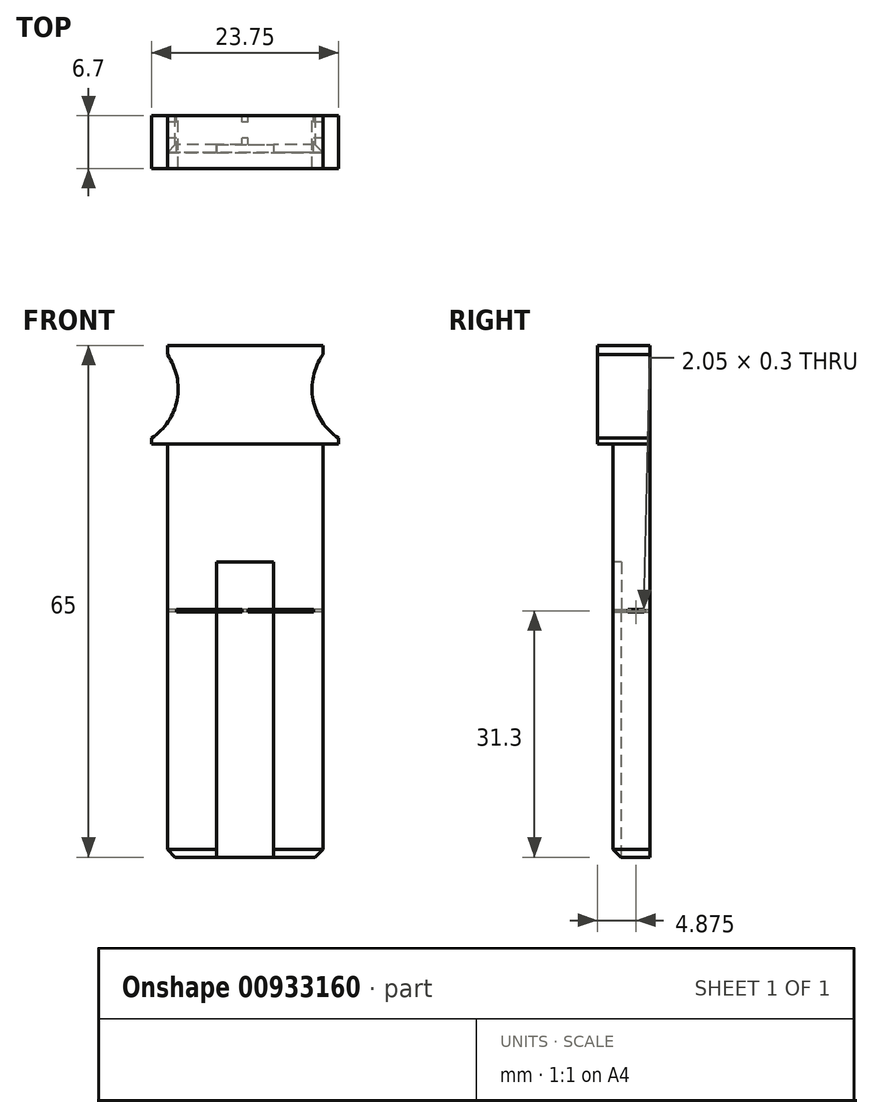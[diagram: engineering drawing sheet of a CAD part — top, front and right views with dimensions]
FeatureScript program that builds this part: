
annotation { "Feature Type Name" : "Feature", "Feature Type Description" : "" }
export const myFeature = defineFeature(function(context is Context, id is Id, definition is map)
    precondition{}
    {
        {
            var Q0;
            Q0=qCreatedBy(makeId("Front.planeOp"),FACE);
            var sketch = newSketch(context, id + "F0", { "sketchPlane" : qUnion([Q0])});
            skLineSegment(sketch, "E0.bottom", {"start": v(0, 0) * mm, "end": v(19.75, 0) * mm});
            skLineSegment(sketch, "E0.top", {"start": v(0, 65) * mm, "end": v(19.75, 65) * mm});
            skLineSegment(sketch, "E0.left", {"start": v(0, 0) * mm, "end": v(0, 65) * mm});
            skLineSegment(sketch, "E0.right", {"start": v(19.75, 0) * mm, "end": v(19.75, 65) * mm});
            skLineSegment(sketch, "E1", {"start": v(9.87, 65) * mm, "end": v(9.87, 0) * mm, "construction": true});
            skPoint(sketch, "E2", {"position": v(9.87, 38.5) * mm});
            skLineSegment(sketch, "E3", {"start": v(-7.67, 31.3) * mm, "end": v(34.9, 31.3) * mm, "construction": true});
            skLineSegment(sketch, "E4", {"start": v(0, 31.15) * mm, "end": v(0, 31.45) * mm});
            skCircle(sketch, "E5", {"center": v(25.88, 59.5) * mm, "radius": 7.5 * mm});
            skCircle(sketch, "E6.MirrorC", {"center": v(-6.13, 59.5) * mm, "radius": 7.5 * mm});
            skLineSegment(sketch, "E7.bottom", {"start": v(0, 31.45) * mm, "end": v(9.47, 31.45) * mm});
            skLineSegment(sketch, "E7.top", {"start": v(0, 31.45) * mm, "end": v(9.47, 31.45) * mm});
            skLineSegment(sketch, "E7.left", {"start": v(0, 31.45) * mm, "end": v(0, 31.45) * mm});
            skLineSegment(sketch, "E7.right", {"start": v(9.47, 31.45) * mm, "end": v(9.47, 31.45) * mm});
            skLineSegment(sketch, "E8", {"start": v(9.47, 31.45) * mm, "end": v(9.47, 31.15) * mm});
            skLineSegment(sketch, "E9", {"start": v(9.47, 31.15) * mm, "end": v(0, 31.15) * mm});
            skLineSegment(sketch, "E10", {"start": v(0, 31.45) * mm, "end": v(0, 31.15) * mm});
            skLineSegment(sketch, "E11.MirrorCS", {"start": v(19.75, 31.45) * mm, "end": v(10.28, 31.45) * mm});
            skLineSegment(sketch, "E12.MirrorCS", {"start": v(10.27, 31.45) * mm, "end": v(10.27, 31.15) * mm});
            skLineSegment(sketch, "E13.MirrorCS", {"start": v(10.28, 31.15) * mm, "end": v(19.75, 31.15) * mm});
            skLineSegment(sketch, "E14.MirrorCS", {"start": v(19.75, 31.45) * mm, "end": v(19.75, 31.15) * mm});
            skLineSegment(sketch, "E15.bottom", {"start": v(0, 52.5) * mm, "end": v(-2, 52.5) * mm});
            skLineSegment(sketch, "E15.top", {"start": v(0, 65.03) * mm, "end": v(-2, 65.03) * mm});
            skLineSegment(sketch, "E15.left", {"start": v(0, 52.5) * mm, "end": v(0, 65.03) * mm});
            skLineSegment(sketch, "E15.right", {"start": v(-2, 52.5) * mm, "end": v(-2, 65.03) * mm});
            skLineSegment(sketch, "E16.MirrorCS", {"start": v(19.75, 65.03) * mm, "end": v(21.75, 65.03) * mm});
            skLineSegment(sketch, "E17.MirrorCS", {"start": v(21.75, 52.5) * mm, "end": v(21.75, 65.03) * mm});
            skLineSegment(sketch, "E18.MirrorCS", {"start": v(19.75, 52.5) * mm, "end": v(21.75, 52.5) * mm});
            skLineSegment(sketch, "E19", {"start": v(1.2, 31.45) * mm, "end": v(1.2, 31.15) * mm});
            skLineSegment(sketch, "E20.MirrorCS", {"start": v(18.55, 31.45) * mm, "end": v(18.55, 31.15) * mm});
            skSolve(sketch);
        }
        {
            var Q0;
            {var subQ4=sQuery(id+"F0.wireOp",EDGE,"E0.bottom");Q0=makeQuery(id+"F0.imprint","IMPRINT",FACE,{"disambiguationData":[TD([[makeQuery(id+"F0.imprint","IMPRINT",EDGE,{"derivedFrom":subQ4}),1.0]])]});}
            var Q1;
            {var subQ0=sQuery(id+"F0.wireOp",EDGE,"E15.bottom");Q1=makeQuery(id+"F0.imprint","IMPRINT",FACE,{"disambiguationData":[TD([[makeQuery(id+"F0.imprint","IMPRINT",EDGE,{"derivedFrom":subQ0}),-1.0]])]});}
            var Q2;
            {var subQ0=sQuery(id+"F0.wireOp",EDGE,"E18.MirrorCS");Q2=makeQuery(id+"F0.imprint","IMPRINT",FACE,{"disambiguationData":[TD([[makeQuery(id+"F0.imprint","IMPRINT",EDGE,{"derivedFrom":subQ0}),1.0]])]});}
            var Q3;
            {var subQ5=sQuery(id+"F0.wireOp",EDGE,"E19");Q3=makeQuery(id+"F0.imprint","IMPRINT",FACE,{"disambiguationData":[TD([[makeQuery(id+"F0.imprint","IMPRINT",EDGE,{"derivedFrom":subQ5}),-1.0]])]});}
            var Q4;
            {var subQ5=sQuery(id+"F0.wireOp",EDGE,"E20.MirrorCS");Q4=makeQuery(id+"F0.imprint","IMPRINT",FACE,{"disambiguationData":[TD([[makeQuery(id+"F0.imprint","IMPRINT",EDGE,{"derivedFrom":subQ5}),1.0]])]});}
            extrude(context, id + "F1", {"entities" : qUnion([Q0, Q1, Q2, Q3, Q4]), "depth" : 4.7 * mm, "offsetDistance" : 25 * mm});
        }
        {
            var Q0;
            Q0=makeQuery(id+"F1.opExtrude","CAP_FACE",FACE,{"disambiguationData":[OSD([sQuery(id+"F0.wireOp",EDGE,"E0.bottom"),sQuery(id+"F0.wireOp",EDGE,"E0.top"),sQuery(id+"F0.wireOp",EDGE,"E0.left"),sQuery(id+"F0.wireOp",EDGE,"E0.right"),sQuery(id+"F0.wireOp",EDGE,"E5"),sQuery(id+"F0.wireOp",EDGE,"E6.MirrorC"),sQuery(id+"F0.wireOp",EDGE,"E7.bottom"),sQuery(id+"F0.wireOp",EDGE,"E8"),sQuery(id+"F0.wireOp",EDGE,"E9"),sQuery(id+"F0.wireOp",EDGE,"E11.MirrorCS"),sQuery(id+"F0.wireOp",EDGE,"E12.MirrorCS"),sQuery(id+"F0.wireOp",EDGE,"E13.MirrorCS"),sQuery(id+"F0.wireOp",EDGE,"E15.bottom"),sQuery(id+"F0.wireOp",EDGE,"E15.right"),sQuery(id+"F0.wireOp",EDGE,"E17.MirrorCS"),sQuery(id+"F0.wireOp",EDGE,"E18.MirrorCS"),sQuery(id+"F0.wireOp",EDGE,"E19"),sQuery(id+"F0.wireOp",EDGE,"E20.MirrorCS")])],"isStart":false});
            var sketch = newSketch(context, id + "F2", { "sketchPlane" : qUnion([Q0])});
            skLineSegment(sketch, "E21", {"start": v(6.27, 37.5) * mm, "end": v(13.47, 37.5) * mm});
            skLineSegment(sketch, "E22", {"start": v(13.47, 37.5) * mm, "end": v(13.47, 2.2) * mm});
            skLineSegment(sketch, "E23", {"start": v(13.47, 2.2) * mm, "end": v(13.47, 2.2) * mm});
            skLineSegment(sketch, "E24", {"start": v(13.47, 2.2) * mm, "end": v(13.47, 0) * mm});
            skLineSegment(sketch, "E25", {"start": v(13.47, 0) * mm, "end": v(6.27, 0) * mm});
            skLineSegment(sketch, "E26", {"start": v(6.27, 0) * mm, "end": v(6.27, 2.2) * mm});
            skLineSegment(sketch, "E27", {"start": v(6.27, 2.2) * mm, "end": v(6.27, 2.2) * mm});
            skLineSegment(sketch, "E28", {"start": v(6.27, 2.2) * mm, "end": v(6.27, 37.5) * mm});
            skLineSegment(sketch, "E29", {"start": v(9.87, 65) * mm, "end": v(9.87, 0) * mm, "construction": true});
            skSolve(sketch);
        }
        {
            var Q0;
            Q0=qSketchRegion(id+"F2",true);
            extrude(context, id + "F3", {"entities" : qUnion([Q0]), "operationType" : NewBodyOperationType.REMOVE, "oppositeDirection" : true, "depth" : 1.05 * mm, "offsetDistance" : 25 * mm});
        }
        {
            var Q0;
            {var subQ0=sQuery(id+"F0.wireOp",EDGE,"E0.right");Q0=makeQuery(id+"F1.opExtrude","SWEPT_FACE",FACE,{"disambiguationData":[OSD([subQ0]),TDD([makeQuery(id+"F0.imprint","IMPRINT",EDGE,{"disambiguationData":[TD([[makeQuery(id+"F0.imprint","INTERSECT",VERTEX,{"derivedFrom":[sQuery(id+"F0.wireOp",EDGE,"E0.top"),subQ0]}),1.0]])],"derivedFrom":subQ0})])]});}
            var sketch = newSketch(context, id + "F4", { "sketchPlane" : qUnion([Q0])});
            skLineSegment(sketch, "E30", {"start": v(-15.64, 31.3) * mm, "end": v(17.74, 31.3) * mm, "construction": true});
            skLineSegment(sketch, "E31", {"start": v(-1, 31.3) * mm, "end": v(0, 32.3) * mm});
            skLineSegment(sketch, "E32", {"start": v(0, 32.3) * mm, "end": v(0, 30.3) * mm});
            skLineSegment(sketch, "E33", {"start": v(0, 30.3) * mm, "end": v(-1, 31.3) * mm});
            skSolve(sketch);
        }
        {
            var Q0;
            Q0=makeQuery(id+"F1.opExtrude","CAP_FACE",FACE,{"disambiguationData":[OSD([sQuery(id+"F0.wireOp",EDGE,"E0.bottom"),sQuery(id+"F0.wireOp",EDGE,"E0.top"),sQuery(id+"F0.wireOp",EDGE,"E0.left"),sQuery(id+"F0.wireOp",EDGE,"E0.right"),sQuery(id+"F0.wireOp",EDGE,"E5"),sQuery(id+"F0.wireOp",EDGE,"E6.MirrorC"),sQuery(id+"F0.wireOp",EDGE,"E7.bottom"),sQuery(id+"F0.wireOp",EDGE,"E8"),sQuery(id+"F0.wireOp",EDGE,"E9"),sQuery(id+"F0.wireOp",EDGE,"E11.MirrorCS"),sQuery(id+"F0.wireOp",EDGE,"E12.MirrorCS"),sQuery(id+"F0.wireOp",EDGE,"E13.MirrorCS"),sQuery(id+"F0.wireOp",EDGE,"E15.bottom"),sQuery(id+"F0.wireOp",EDGE,"E15.right"),sQuery(id+"F0.wireOp",EDGE,"E17.MirrorCS"),sQuery(id+"F0.wireOp",EDGE,"E18.MirrorCS"),sQuery(id+"F0.wireOp",EDGE,"E19"),sQuery(id+"F0.wireOp",EDGE,"E20.MirrorCS")])],"isStart":false});
            var sketch = newSketch(context, id + "F5", { "sketchPlane" : qUnion([Q0])});
            skLineSegment(sketch, "E34", {"start": v(0, 52.5) * mm, "end": v(19.75, 52.5) * mm});
            skSolve(sketch);
        }
        {
            var Q0;
            Q0=makeQuery(id+"F5.imprint","IMPRINT",FACE,{"disambiguationData":[TD([[makeQuery(id+"F5.imprint","IMPRINT",EDGE,{"derivedFrom":sQuery(id+"F5.wireOp",EDGE,"E34")}),1.0]])]});
            extrude(context, id + "F6", {"entities" : qUnion([Q0]), "operationType" : NewBodyOperationType.ADD, "depth" : 2 * mm, "offsetDistance" : 25 * mm});
        }
        {
            var Q0;
            Q0=makeQuery(id+"F1.opExtrude","SWEPT_EDGE",EDGE,{"disambiguationData":[OSD([sQuery(id+"F0.wireOp",EDGE,"E0.bottom"),sQuery(id+"F0.wireOp",EDGE,"E0.left")])]});
            var Q1;
            Q1=makeQuery(id+"F1.opExtrude","SWEPT_EDGE",EDGE,{"disambiguationData":[OSD([sQuery(id+"F0.wireOp",EDGE,"E0.bottom"),sQuery(id+"F0.wireOp",EDGE,"E0.right")])]});
            var Q2;
            {var subQ0=sQuery(id+"F0.wireOp",EDGE,"E0.bottom");Q2=makeQuery(id+"F3.boolean.opBoolean","SPLIT",EDGE,{"disambiguationData":[TD([makeQuery(id+"F3.opExtrude","SWEPT_FACE",FACE,{"disambiguationData":[OSD([sQuery(id+"F2.wireOp",EDGE,"E26"),sQuery(id+"F2.wireOp",EDGE,"E28")])]})])],"derivedFrom":makeQuery(id+"F1.opExtrude","CAP_EDGE",EDGE,{"disambiguationData":[OSD([subQ0])],"isStart":false})});}
            var Q3;
            {var subQ0=sQuery(id+"F0.wireOp",EDGE,"E0.bottom");Q3=makeQuery(id+"F3.boolean.opBoolean","SPLIT",EDGE,{"disambiguationData":[TD([makeQuery(id+"F3.opExtrude","SWEPT_FACE",FACE,{"disambiguationData":[OSD([sQuery(id+"F2.wireOp",EDGE,"E22"),sQuery(id+"F2.wireOp",EDGE,"E24")])]})])],"derivedFrom":makeQuery(id+"F1.opExtrude","CAP_EDGE",EDGE,{"disambiguationData":[OSD([subQ0])],"isStart":false})});}
            var Q4;
            Q4=makeQuery(id+"F3.boolean.opBoolean","COPY",EDGE,{"derivedFrom":makeQuery(id+"F3.opExtrude","CAP_EDGE",EDGE,{"disambiguationData":[OSD([sQuery(id+"F2.wireOp",EDGE,"E25")])],"isStart":false})});
            chamfer(context, id + "F7", {"entities" : qUnion([Q0, Q1, Q2, Q3, Q4]), "width" : 1 * mm, "tangentPropagation" : true});
        }
        {
            var Q0;
            Q0=makeQuery(id+"F1.opExtrude","SWEPT_FACE",FACE,{"disambiguationData":[OSD([sQuery(id+"F0.wireOp",EDGE,"E8")])]});
            var sketch = newSketch(context, id + "F8", { "sketchPlane" : qUnion([Q0])});
            skLineSegment(sketch, "E35.bottom", {"start": v(0.8, 31.45) * mm, "end": v(2.85, 31.45) * mm});
            skLineSegment(sketch, "E35.top", {"start": v(0.8, 31.15) * mm, "end": v(2.85, 31.15) * mm});
            skLineSegment(sketch, "E35.left", {"start": v(0.8, 31.45) * mm, "end": v(0.8, 31.15) * mm});
            skLineSegment(sketch, "E35.right", {"start": v(2.85, 31.45) * mm, "end": v(2.85, 31.15) * mm});
            skLineSegment(sketch, "E36", {"start": v(0, 31.45) * mm, "end": v(0.8, 31.45) * mm, "construction": true});
            skLineSegment(sketch, "E37", {"start": v(2.85, 31.45) * mm, "end": v(3.65, 31.45) * mm, "construction": true});
            skSolve(sketch);
        }
        {
            var Q0;
            Q0=qSketchRegion(id+"F8",true);
            extrude(context, id + "F9", {"entities" : qUnion([Q0]), "operationType" : NewBodyOperationType.REMOVE, "endBound" : BoundingType.SYMMETRIC, "oppositeDirection" : true, "depth" : 250 * mm, "offsetDistance" : 25 * mm});
        }
    });
